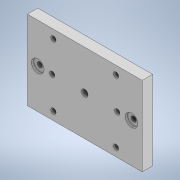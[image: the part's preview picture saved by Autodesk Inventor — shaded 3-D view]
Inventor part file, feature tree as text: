
AUTODESK INVENTOR PART (.ipt)
format: ipt  version: 2022.2 (Build 262287030, 287C)  size: 131,072 bytes
history: native  units: in
note: dims shown in document units (in); Inventor stores cm internally (conversion verified against a paired STEP export)
features: sketch x4, hole x3, extrude x1, projected_geometry x1
ambient origin geometry x8: Origin, YZ Plane, XZ Plane, XY Plane, X Axis, Y Axis, Z Axis, Center Point
bodies: Solid1 (feature_tree)
feature tree (9):
  extrude  "Extrusion1"  Depth=1.4961in
  hole  "Hole1"  [1 undecoded]
  hole  "Hole2"  [1 undecoded]
  hole  "Hole3"  [1 undecoded]
  sketch  "Sketch1"  dims[d0=0.1969in d1=0.0in d2=1.4961in]
  sketch  "Sketch2"  dims[d3=2.1654in d4=0.5906in]
  projected_geometry  "Projected Loop1"
  sketch  "Sketch3"  dims[d5=0.5906in d34=0.7874in d36=1.1811in d37=0.3937in d39=0.3937in]
  sketch  "Sketch4"  dims[d41=0.7874in d43=1.1811in d44=0.3937in d46=0.3937in d48=0.7874in d50=0.6142in d51=0.3937in d53=0.3937in d55=0.7874in d57=0.6142in d58=0.3937in d60=0.3937in d62=0.0984in d63=0.2953in d64=0.1476in d65=0.0984in d66=90.0deg d67=0.3937in d68=0.8108in d69=0.125in d70=0.2953in d71=0.1476in d72=0.0984in d73=90.0deg d74=0.3937in d75=0.8108in d76=0.1969in d77=0.1969in d78=0.0968in d79=0.2362in d80=0.2362in d81=0.0394in d82=90.0deg d83=0.3937in d84=0.8108in d89=0.8858in]
note: 3 required parameter values undecoded (feature->parameter linkage not recoverable at this tier; creation-order binding heuristic only, values carry confidence <= 0.55)
